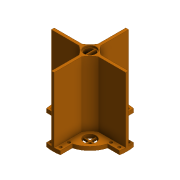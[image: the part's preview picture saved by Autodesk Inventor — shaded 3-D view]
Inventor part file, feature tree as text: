
AUTODESK INVENTOR PART (.ipt)
format: ipt  version: 2020.3 (Build 243373000, 373)  size: 317,440 bytes
history: native  units: mm
features: extrude x10, sketch x7, pattern_circular x3
ambient origin geometry x8: Origin, YZ Plane, XZ Plane, XY Plane, X Axis, Y Axis, Z Axis, Center Point
bodies: Solid1 (feature_tree)
feature tree (20):
  extrude  "Extrusion1"  Depth=4.0mm TaperAngle=0.0deg
  extrude  "Extrusion2"  Depth=3.0mm
  sketch  "Sketch5"  dims[d7=3.0mm d8=3.0mm]
  extrude  "Extrusion5"  Depth=3.0mm
  extrude  "Extrusion6"  Depth=70.0mm
  pattern_circular  "Circular Pattern1"  Count=4 Angle=360.0deg
  sketch  "Sketch8"  dims[d9=70.0mm d10=0.0mm d20=13.0mm]
  extrude  "Extrusion13"  Depth=1.5mm
  extrude  "Extrusion14"  Depth=1.5mm
  pattern_circular  "Circular Pattern3"  [2 undecoded]
  extrude  "Extrusion15"  Depth=3.0mm
  sketch  "Sketch10"  dims[d25=8.0mm]
  extrude  "Extrusion17"  Depth=3.0mm
  extrude  "Extrusion18"  Depth=1.5mm
  extrude  "Extrusion19"  Depth=24.665113mm
  pattern_circular  "Circular Pattern4"  Angle=45.0deg  [1 undecoded]
  sketch  "Sketch12"  dims[d28=4.0mm d29=0.0mm d33=40.0mm d34=360.0deg d58=1.5mm d59=1.5mm d84=15.0mm d85=13.0mm d86=11.0mm d87=1.5mm d88=24.665113mm d89=45.0deg d90=40.0mm d92=360.0deg d94=13.0mm d95=0.0mm d96=10.0mm d97=0.0mm d98=40.0mm d99=360.0deg d101=2.0mm d102=0.0mm d106=55.0mm d107=80.0mm d108=10.0mm d109=0.0mm d110=10.0mm d111=0.0mm d112=6.0mm d113=3.0mm d114=7.5mm d115=3.0mm d116=36.0mm d117=36.0mm d118=3.0mm d119=3.0mm d120=6.25mm d121=0.0mm d122=40.0mm d123=360.0deg d125=3.0mm d75=0.5mm d76=0.872665mm d77=0.5mm d78=0.872665mm]
  sketch  "Sketch1"  dims[d0=60.0mm d1=4.0mm d2=0.0mm]
  sketch  "Sketch2"  dims[d5=3.0mm d6=3.0mm]
  sketch  "Sketch11"  dims[d26=2.0mm d27=0.0mm]
note: 3 required parameter values undecoded (feature->parameter linkage not recoverable at this tier; creation-order binding heuristic only, values carry confidence <= 0.55)
